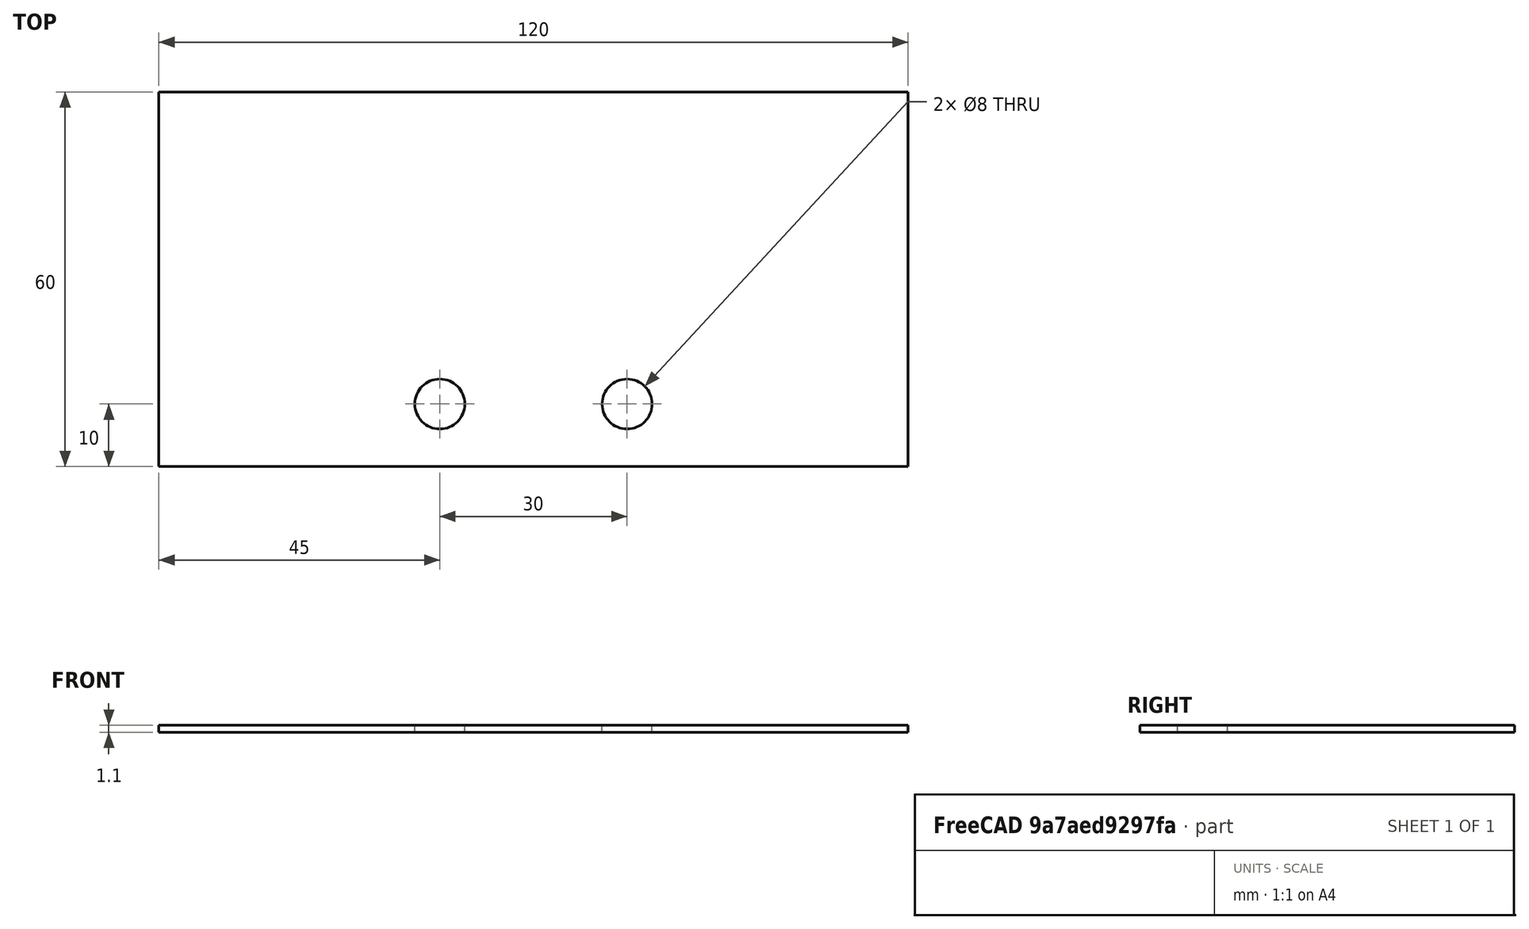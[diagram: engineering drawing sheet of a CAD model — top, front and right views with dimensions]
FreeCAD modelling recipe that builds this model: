
FCSTD DOCUMENT  (FreeCAD 0.17R13541 (Git))
Label: backplate
License: All rights reserved
LicenseURL: http://en.wikipedia.org/wiki/All_rights_reserved
objects: Part::Cylinder×2, Part::Cut×2, Part::Box×1
note: 5 computed .brp shape members not serialized (recipe doc carries the construction recipe); baked Part::Feature solids carry a one-line shape summary decoded from their .brp

FEATURE [Part::Box] Box  label="Cube"
  AttacherType = Attacher::AttachEngine3D
  Height = 1.1
  Length = 120
  Width = 60
FEATURE [Part::Cylinder] Cylinder
  Angle = 360
  AttacherType = Attacher::AttachEngine3D
  Height = 1.1
  Placement = pos=(45,10,0) rot=(0.975957,0.216879,0.021688;0rad)
  Radius = 4
FEATURE [Part::Cylinder] Cylinder001
  Angle = 360
  AttacherType = Attacher::AttachEngine3D
  Height = 1.1
  Placement = pos=(75,10,0) rot=(0.975958,0.216879,0.021688;0rad)
  Radius = 4
FEATURE [Part::Cut] Cut
  Base = -> Box
  Tool = -> Cylinder
FEATURE [Part::Cut] Cut001
  Base = -> Cut
  Tool = -> Cylinder001
